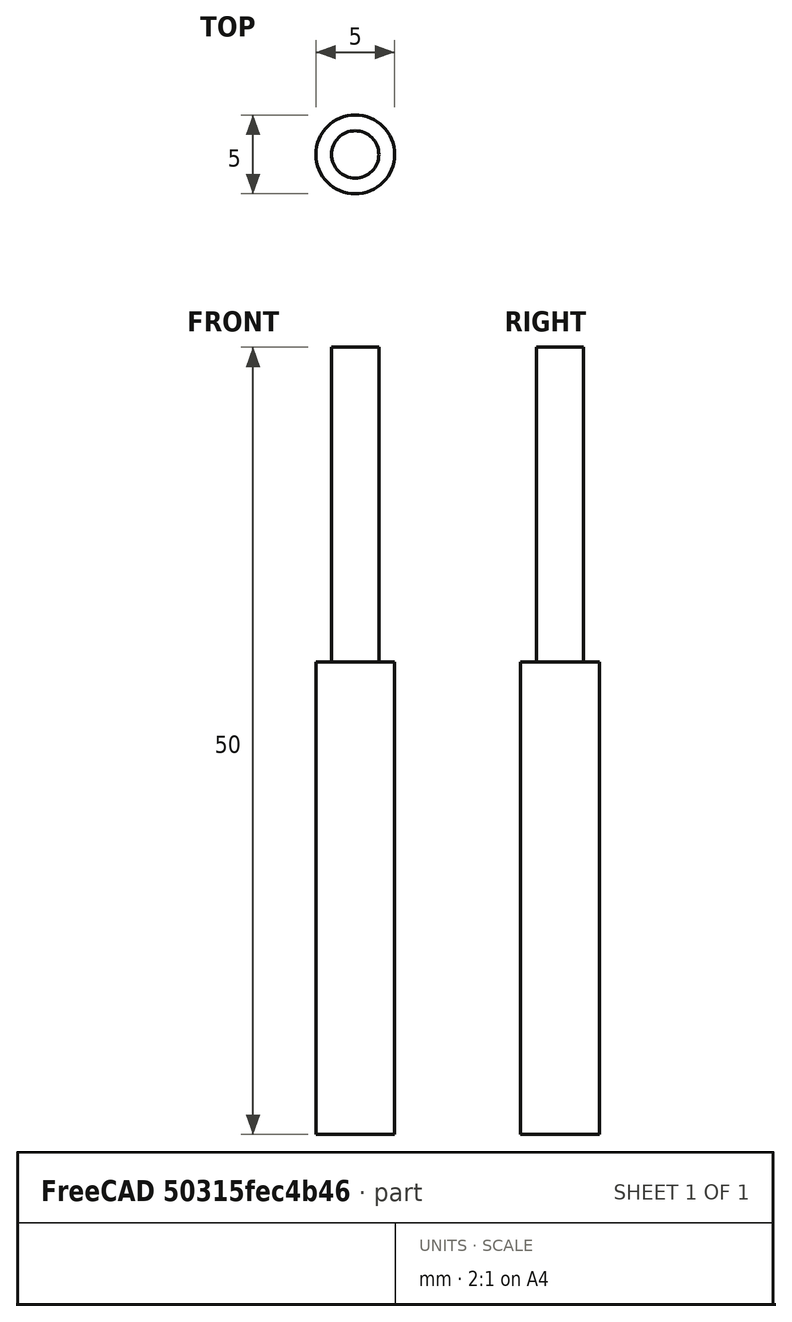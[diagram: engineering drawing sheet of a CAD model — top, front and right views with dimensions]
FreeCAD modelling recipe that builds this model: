
FCSTD DOCUMENT  (FreeCAD 1.0R39109 (Git))
Label: endmill
License: Creative Commons Attribution 4.0
LicenseURL: https://creativecommons.org/licenses/by/4.0/
objects: Sketcher::SketchObject×1, PartDesign::Revolution×1, App::FeaturePython×1, PartDesign::Body×1
note: 6 computed .brp shape members not serialized (recipe doc carries the construction recipe); baked Part::Feature solids carry a one-line shape summary decoded from their .brp

FEATURE [Sketcher::SketchObject] Sketch
  ArcFitTolerance = 0
  AttachmentSupport = -> [XZ_Plane]
  FullyConstrained = true
  MakeInternals = false
  MapMode = 5
  Placement = pos=(0,0,0) rot=(1,0,0;1.5708rad)
  expr: Constraints[10] = <<Attributes>>.Length
  expr: Constraints[16] = <<Attributes>>.ShankDiameter
  expr: Constraints[18] = <<Attributes>>.CuttingEdgeHeight
  expr: Constraints[9] = <<Attributes>>.Diameter
  sketch-geometry (8):
    g0: LineSegment StartX=0 StartY=50 StartZ=0 EndX=0 EndY=0 EndZ=0
    g1: LineSegment StartX=0 StartY=0 StartZ=0 EndX=2.5 EndY=0 EndZ=0
    g2: LineSegment StartX=2.5 StartY=0 StartZ=0 EndX=2.5 EndY=30 EndZ=0
    g3: LineSegment StartX=1.5 StartY=50 StartZ=0 EndX=0 EndY=50 EndZ=0
    g4: LineSegment [constr] StartX=2.5 StartY=0 StartZ=0 EndX=-2.5 EndY=0 EndZ=0
    g5: LineSegment StartX=1.5 StartY=29.99 StartZ=0 EndX=2.5 EndY=30 EndZ=0
    g6: LineSegment StartX=1.5 StartY=50 StartZ=0 EndX=1.5 EndY=29.99 EndZ=0
    g7: LineSegment [constr] StartX=-1.5 StartY=50 StartZ=0 EndX=1.5 EndY=50 EndZ=0
  constraints (21):
    c: Vertical(g0)
    c: Coincident(g0,g1)
    c: Horizontal(g1)
    c: Coincident(g1,g2)
    c: Vertical(g2)
    c: Horizontal(g3)
    c: Coincident(g0,g3)
    c: Coincident(g4,g1)
    c: Symmetric(g1,g4,g0)
    c: DistanceX(g4,g4) = 5
    c: DistanceY(g2,g3) = 50
    c: Coincident(g2,g5)
    c: Vertical(g6)
    c: Coincident(g3,g6)
    c: Symmetric(g7,g7,g0)
    c: Coincident(g7,g3)
    c: DistanceX(g7,g7) = 3
    c: Coincident(g5,g6)
    c: DistanceY(g2) = 30
    c: Coincident(g0,g-1)
    c: DistanceY(g5,g2) = 0.01
FEATURE [PartDesign::Revolution] Revolution
  AllowMultiFace = false
  Angle = 360
  Angle2 = 60
  Axis = (0,2e-16,1)
  Base = (0,0,0)
  Placement = pos=(0,0,0) rot=(1,0,0;1.5708rad)
  Profile = -> Sketch
  ReferenceAxis = -> Sketch [V_Axis]
  Reversed = true
  Suppressed = false
  Type = 0
FEATURE [App::FeaturePython] PropertyBag  label="Attributes"  # WARN: FeaturePython — macro-defined, semantics opaque (R4)
  CustomPropertyGroups = 0
  CuttingEdgeHeight = 30
  Diameter = 5
  Flutes = 4
  Length = 50
  ShankDiameter = 3
FEATURE [PartDesign::Body] Body  label="Endmill"
  AllowCompound = false
  Group = -> [Sketch,Revolution,PropertyBag]
  Origin = -> Origin
  Tip = -> Revolution
